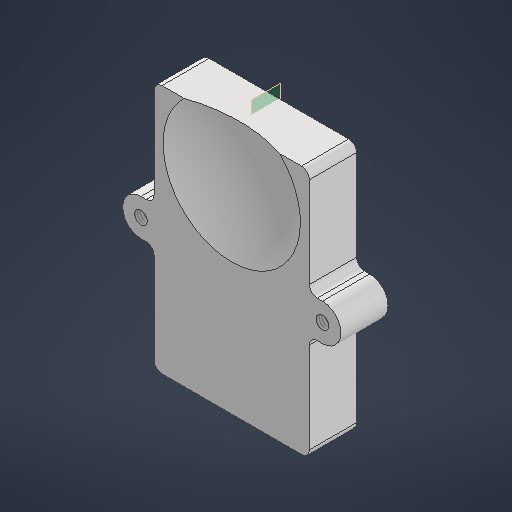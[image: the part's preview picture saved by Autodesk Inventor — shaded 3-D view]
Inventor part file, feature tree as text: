
AUTODESK INVENTOR PART (.ipt)
format: ipt  version: 2025.1 (Build 291241020, 241B)  size: 326,656 bytes
history: native  units: mm
features: reference x42, sketch x5, other x4, extrude x3, projected_geometry x3, plane x1, revolve x1, shell x1, hole x1
ambient origin geometry x8: Origin, YZ Plane, XZ Plane, XY Plane, X Axis, Y Axis, Z Axis, Center Point
bodies: Solid1 (feature_tree)
feature tree (61):
  extrude  "Extrusion1"  Depth=9.0mm
  plane  "Work Plane1"
  revolve  "Revolution1"  Angle=90.0deg
  shell  "Shell1"  Thickness=1.0mm
  extrude  "Extrusion2"  Depth=2.0mm
  hole  "Hole1"  [1 undecoded]
  extrude  "Extrusion3"  [1 undecoded]
  sketch  "Sketch1"  dims[d0=9.0mm d1=0.0mm d2=60.0mm]
  reference  "Reference1"
  reference  "Reference2"
  reference  "Reference3"
  reference  "Reference4"
  reference  "Reference5"
  reference  "Reference6"
  reference  "Reference7"
  reference  "Reference8"
  reference  "Reference9"
  reference  "Reference10"
  reference  "Reference11"
  reference  "Reference12"
  reference  "Reference13"
  reference  "Reference14"
  reference  "Reference15"
  reference  "Reference16"
  reference  "Reference17"
  reference  "Reference18"
  reference  "Reference19"
  reference  "Reference20"
  reference  "Reference21"
  reference  "Reference22"
  reference  "Reference23"
  reference  "Reference24"
  reference  "Reference25"
  reference  "Reference26"
  reference  "Reference27"
  reference  "Reference28"
  reference  "Reference29"
  reference  "Reference30"
  reference  "Reference31"
  reference  "Reference32"
  reference  "Reference33"
  reference  "Reference34"
  reference  "Reference35"
  reference  "Reference36"
  reference  "Reference37"
  sketch  "Sketch2"  dims[d3=27.0mm d4=90.0deg d5=1.0mm]
  sketch  "Sketch4"  dims[d6=5.0mm d7=0.0mm]
  projected_geometry  "Projected Loop1"
  sketch  "Sketch5"  dims[d8=2.459mm d9=6.0mm d10=6.5mm d11=3.0mm d12=90.0deg d13=8.0mm d14=20.594885mm d15=2.0mm]
  reference  "Reference39"
  reference  "Reference40"
  reference  "Reference41"
  projected_geometry  "Projected Loop2"
  sketch  "Sketch6"  dims[d16=9.0mm d17=0.0mm]
  projected_geometry  "Projected Loop3"
  reference  "Reference42"
  reference  "Reference43"
  other  "<userpath>\Documents\PassiveSonar\MicModule.iam"
  other  "MicModule.iam"
  other  "Backplane:1"
  other  "PassiveSonar:1"
note: 2 required parameter values undecoded (feature->parameter linkage not recoverable at this tier; creation-order binding heuristic only, values carry confidence <= 0.55)
